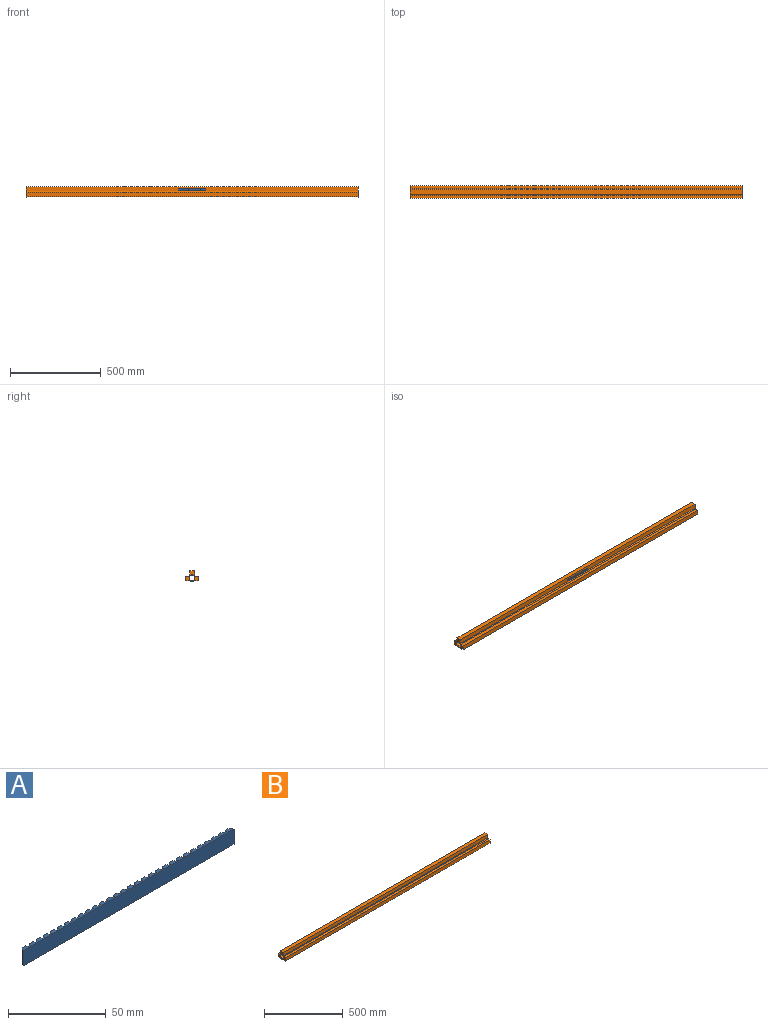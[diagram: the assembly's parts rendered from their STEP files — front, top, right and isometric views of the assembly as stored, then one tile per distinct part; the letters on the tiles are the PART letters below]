
ASSEMBLY  parts=2 mates=1
PART A: 126 faces, bbox 152.4x2.3x9.5 mm
  f0: plane 9.53x2.51mm, normal (0,1,0), area 24mm2, adj f33,f34,f121,f125
  f1: plane 9.53x2.51mm, normal (0,1,0), area 24mm2, adj f33,f34,f118,f123
  f2: plane 9.53x2.51mm, normal (0,1,0), area 24mm2, adj f33,f34,f115,f120
  f3: plane 9.53x2.51mm, normal (0,1,0), area 24mm2, adj f33,f34,f112,f117
  f4: plane 9.53x2.51mm, normal (0,1,0), area 24mm2, adj f33,f34,f109,f114
  f5: plane 9.53x2.51mm, normal (0,1,0), area 24mm2, adj f33,f34,f106,f111
  f6: plane 9.53x2.51mm, normal (0,1,0), area 24mm2, adj f33,f34,f103,f108
  f7: plane 9.53x2.51mm, normal (0,1,0), area 24mm2, adj f33,f34,f100,f105
  f8: plane 9.53x2.51mm, normal (0,1,0), area 24mm2, adj f33,f34,f97,f102
  f9: plane 9.53x2.51mm, normal (0,1,0), area 24mm2, adj f33,f34,f94,f99
  f10: plane 9.53x2.51mm, normal (0,1,0), area 24mm2, adj f33,f34,f91,f96
  f11: plane 9.53x2.51mm, normal (0,1,0), area 24mm2, adj f33,f34,f88,f93
  f12: plane 9.53x2.51mm, normal (0,1,0), area 24mm2, adj f33,f34,f85,f90
  f13: plane 9.53x2.51mm, normal (0,1,0), area 24mm2, adj f33,f34,f82,f87
  f14: plane 9.53x2.51mm, normal (0,1,0), area 24mm2, adj f33,f34,f79,f84
  f15: plane 9.53x2.51mm, normal (0,1,0), area 24mm2, adj f33,f34,f76,f81
  f16: plane 9.53x2.51mm, normal (0,1,0), area 24mm2, adj f33,f34,f73,f78
  f17: plane 9.53x2.51mm, normal (0,1,0), area 24mm2, adj f33,f34,f70,f75
  f18: plane 9.53x2.51mm, normal (0,1,0), area 24mm2, adj f33,f34,f67,f72
  f19: plane 9.53x2.51mm, normal (0,1,0), area 24mm2, adj f33,f34,f64,f69
  f20: plane 9.53x2.51mm, normal (0,1,0), area 24mm2, adj f33,f34,f61,f66
  f21: plane 9.53x2.51mm, normal (0,1,0), area 24mm2, adj f33,f34,f58,f63
  f22: plane 9.53x2.51mm, normal (0,1,0), area 24mm2, adj f33,f34,f55,f60
  f23: plane 9.53x2.51mm, normal (0,1,0), area 24mm2, adj f33,f34,f52,f57
  f24: plane 9.53x2.51mm, normal (0,1,0), area 24mm2, adj f33,f34,f49,f54
  f25: plane 9.53x2.51mm, normal (0,1,0), area 24mm2, adj f33,f34,f46,f51
  f26: plane 9.53x2.51mm, normal (0,1,0), area 24mm2, adj f33,f34,f43,f48
  f27: plane 9.53x2.51mm, normal (0,1,0), area 24mm2, adj f33,f34,f40,f45
  f28: plane 9.53x2.51mm, normal (0,1,0), area 24mm2, adj f33,f34,f37,f42
  f29: plane 9.53x1.02mm, normal (-1,0,0), area 9.7mm2, adj f30,f33,f34,f35
  f30: plane 152.4x9.53mm, normal (0,-1,0), area 1451.6mm2, adj f29,f31,f33,f34
  f31: plane 9.53x1.02mm, normal (1,0,0), area 9.7mm2, adj f30,f33,f34,f124
  f32: plane 9.53x2.51mm, normal (0,1,0), area 24mm2, adj f33,f34,f36,f39
  f33: plane 152.4x2.29mm, normal (0,0,1), area 273.2mm2, adj f0,f1,f2,f3,f4,f5,f6,f7
  f34: plane 152.4x2.29mm, normal (0,0,-1), area 273.2mm2, adj f0,f1,f2,f3,f4,f5,f6,f7
  f35: plane 9.53x0.69mm, normal (0,1,0), area 6.6mm2, adj f29,f33,f34,f36
  f36: plane 9.53x1.27mm, normal (-0.91,0.42,0), area 13.3mm2, adj f32,f33,f34,f35
  f37: plane 9.53x1.27mm, normal (-0.91,0.42,0), area 13.3mm2, adj f28,f33,f34,f38
  f38: plane 9.53x1.38mm, normal (0,1,0), area 13.2mm2, adj f33,f34,f37,f39
  f39: plane 9.53x1.27mm, normal (0.91,0.42,0), area 13.3mm2, adj f32,f33,f34,f38
  f40: plane 9.53x1.27mm, normal (-0.91,0.42,0), area 13.3mm2, adj f27,f33,f34,f41
  f41: plane 9.53x1.38mm, normal (0,1,0), area 13.2mm2, adj f33,f34,f40,f42
  f42: plane 9.53x1.27mm, normal (0.91,0.42,0), area 13.3mm2, adj f28,f33,f34,f41
  f43: plane 9.53x1.27mm, normal (-0.91,0.42,0), area 13.3mm2, adj f26,f33,f34,f44
  f44: plane 9.53x1.38mm, normal (0,1,0), area 13.2mm2, adj f33,f34,f43,f45
  f45: plane 9.53x1.27mm, normal (0.91,0.42,0), area 13.3mm2, adj f27,f33,f34,f44
  f46: plane 9.53x1.27mm, normal (-0.91,0.42,0), area 13.3mm2, adj f25,f33,f34,f47
  f47: plane 9.53x1.38mm, normal (0,1,0), area 13.2mm2, adj f33,f34,f46,f48
  f48: plane 9.53x1.27mm, normal (0.91,0.42,0), area 13.3mm2, adj f26,f33,f34,f47
  f49: plane 9.53x1.27mm, normal (-0.91,0.42,0), area 13.3mm2, adj f24,f33,f34,f50
  f50: plane 9.53x1.38mm, normal (0,1,0), area 13.2mm2, adj f33,f34,f49,f51
  f51: plane 9.53x1.27mm, normal (0.91,0.42,0), area 13.3mm2, adj f25,f33,f34,f50
  f52: plane 9.53x1.27mm, normal (-0.91,0.42,0), area 13.3mm2, adj f23,f33,f34,f53
  f53: plane 9.53x1.38mm, normal (0,1,0), area 13.2mm2, adj f33,f34,f52,f54
  f54: plane 9.53x1.27mm, normal (0.91,0.42,0), area 13.3mm2, adj f24,f33,f34,f53
  f55: plane 9.53x1.27mm, normal (-0.91,0.42,0), area 13.3mm2, adj f22,f33,f34,f56
  f56: plane 9.53x1.38mm, normal (0,1,0), area 13.2mm2, adj f33,f34,f55,f57
  f57: plane 9.53x1.27mm, normal (0.91,0.42,0), area 13.3mm2, adj f23,f33,f34,f56
  f58: plane 9.53x1.27mm, normal (-0.91,0.42,0), area 13.3mm2, adj f21,f33,f34,f59
  f59: plane 9.53x1.38mm, normal (0,1,0), area 13.2mm2, adj f33,f34,f58,f60
  f60: plane 9.53x1.27mm, normal (0.91,0.42,0), area 13.3mm2, adj f22,f33,f34,f59
  f61: plane 9.53x1.27mm, normal (-0.91,0.42,0), area 13.3mm2, adj f20,f33,f34,f62
  f62: plane 9.53x1.38mm, normal (0,1,0), area 13.2mm2, adj f33,f34,f61,f63
  f63: plane 9.53x1.27mm, normal (0.91,0.42,0), area 13.3mm2, adj f21,f33,f34,f62
  f64: plane 9.53x1.27mm, normal (-0.91,0.42,0), area 13.3mm2, adj f19,f33,f34,f65
  f65: plane 9.53x1.38mm, normal (0,1,0), area 13.2mm2, adj f33,f34,f64,f66
  f66: plane 9.53x1.27mm, normal (0.91,0.42,0), area 13.3mm2, adj f20,f33,f34,f65
  f67: plane 9.53x1.27mm, normal (-0.91,0.42,0), area 13.3mm2, adj f18,f33,f34,f68
  f68: plane 9.53x1.38mm, normal (0,1,0), area 13.2mm2, adj f33,f34,f67,f69
  f69: plane 9.53x1.27mm, normal (0.91,0.42,0), area 13.3mm2, adj f19,f33,f34,f68
  f70: plane 9.53x1.27mm, normal (-0.91,0.42,0), area 13.3mm2, adj f17,f33,f34,f71
  f71: plane 9.53x1.38mm, normal (0,1,0), area 13.2mm2, adj f33,f34,f70,f72
  f72: plane 9.53x1.27mm, normal (0.91,0.42,0), area 13.3mm2, adj f18,f33,f34,f71
  f73: plane 9.53x1.27mm, normal (-0.91,0.42,0), area 13.3mm2, adj f16,f33,f34,f74
  f74: plane 9.53x1.38mm, normal (0,1,0), area 13.2mm2, adj f33,f34,f73,f75
  f75: plane 9.53x1.27mm, normal (0.91,0.42,0), area 13.3mm2, adj f17,f33,f34,f74
  f76: plane 9.53x1.27mm, normal (-0.91,0.42,0), area 13.3mm2, adj f15,f33,f34,f77
  f77: plane 9.53x1.38mm, normal (0,1,0), area 13.2mm2, adj f33,f34,f76,f78
  f78: plane 9.53x1.27mm, normal (0.91,0.42,0), area 13.3mm2, adj f16,f33,f34,f77
  f79: plane 9.53x1.27mm, normal (-0.91,0.42,0), area 13.3mm2, adj f14,f33,f34,f80
  f80: plane 9.53x1.38mm, normal (0,1,0), area 13.2mm2, adj f33,f34,f79,f81
  f81: plane 9.53x1.27mm, normal (0.91,0.42,0), area 13.3mm2, adj f15,f33,f34,f80
  f82: plane 9.53x1.27mm, normal (-0.91,0.42,0), area 13.3mm2, adj f13,f33,f34,f83
  f83: plane 9.53x1.38mm, normal (0,1,0), area 13.2mm2, adj f33,f34,f82,f84
  f84: plane 9.53x1.27mm, normal (0.91,0.42,0), area 13.3mm2, adj f14,f33,f34,f83
  f85: plane 9.53x1.27mm, normal (-0.91,0.42,0), area 13.3mm2, adj f12,f33,f34,f86
  f86: plane 9.53x1.38mm, normal (0,1,0), area 13.2mm2, adj f33,f34,f85,f87
  f87: plane 9.53x1.27mm, normal (0.91,0.42,0), area 13.3mm2, adj f13,f33,f34,f86
  f88: plane 9.53x1.27mm, normal (-0.91,0.42,0), area 13.3mm2, adj f11,f33,f34,f89
  f89: plane 9.53x1.38mm, normal (0,1,0), area 13.2mm2, adj f33,f34,f88,f90
  f90: plane 9.53x1.27mm, normal (0.91,0.42,0), area 13.3mm2, adj f12,f33,f34,f89
  f91: plane 9.53x1.27mm, normal (-0.91,0.42,0), area 13.3mm2, adj f10,f33,f34,f92
  f92: plane 9.53x1.38mm, normal (0,1,0), area 13.2mm2, adj f33,f34,f91,f93
  f93: plane 9.53x1.27mm, normal (0.91,0.42,0), area 13.3mm2, adj f11,f33,f34,f92
  f94: plane 9.53x1.27mm, normal (-0.91,0.42,0), area 13.3mm2, adj f9,f33,f34,f95
  f95: plane 9.53x1.38mm, normal (0,1,0), area 13.2mm2, adj f33,f34,f94,f96
  f96: plane 9.53x1.27mm, normal (0.91,0.42,0), area 13.3mm2, adj f10,f33,f34,f95
  f97: plane 9.53x1.27mm, normal (-0.91,0.42,0), area 13.3mm2, adj f8,f33,f34,f98
  f98: plane 9.53x1.38mm, normal (0,1,0), area 13.2mm2, adj f33,f34,f97,f99
  f99: plane 9.53x1.27mm, normal (0.91,0.42,0), area 13.3mm2, adj f9,f33,f34,f98
  f100: plane 9.53x1.27mm, normal (-0.91,0.42,0), area 13.3mm2, adj f7,f33,f34,f101
  f101: plane 9.53x1.38mm, normal (0,1,0), area 13.2mm2, adj f33,f34,f100,f102
  f102: plane 9.53x1.27mm, normal (0.91,0.42,0), area 13.3mm2, adj f8,f33,f34,f101
  f103: plane 9.53x1.27mm, normal (-0.91,0.42,0), area 13.3mm2, adj f6,f33,f34,f104
  f104: plane 9.53x1.38mm, normal (0,1,0), area 13.2mm2, adj f33,f34,f103,f105
  f105: plane 9.53x1.27mm, normal (0.91,0.42,0), area 13.3mm2, adj f7,f33,f34,f104
  f106: plane 9.53x1.27mm, normal (-0.91,0.42,0), area 13.3mm2, adj f5,f33,f34,f107
  f107: plane 9.53x1.38mm, normal (0,1,0), area 13.2mm2, adj f33,f34,f106,f108
  f108: plane 9.53x1.27mm, normal (0.91,0.42,0), area 13.3mm2, adj f6,f33,f34,f107
  f109: plane 9.53x1.27mm, normal (-0.91,0.42,0), area 13.3mm2, adj f4,f33,f34,f110
  f110: plane 9.53x1.38mm, normal (0,1,0), area 13.2mm2, adj f33,f34,f109,f111
  f111: plane 9.53x1.27mm, normal (0.91,0.42,0), area 13.3mm2, adj f5,f33,f34,f110
  f112: plane 9.53x1.27mm, normal (-0.91,0.42,0), area 13.3mm2, adj f3,f33,f34,f113
  f113: plane 9.53x1.38mm, normal (0,1,0), area 13.2mm2, adj f33,f34,f112,f114
  f114: plane 9.53x1.27mm, normal (0.91,0.42,0), area 13.3mm2, adj f4,f33,f34,f113
  f115: plane 9.53x1.27mm, normal (-0.91,0.42,0), area 13.3mm2, adj f2,f33,f34,f116
  f116: plane 9.53x1.38mm, normal (0,1,0), area 13.2mm2, adj f33,f34,f115,f117
  f117: plane 9.53x1.27mm, normal (0.91,0.42,0), area 13.3mm2, adj f3,f33,f34,f116
  f118: plane 9.53x1.27mm, normal (-0.91,0.42,0), area 13.3mm2, adj f1,f33,f34,f119
  f119: plane 9.53x1.38mm, normal (0,1,0), area 13.2mm2, adj f33,f34,f118,f120
  f120: plane 9.53x1.27mm, normal (0.91,0.42,0), area 13.3mm2, adj f2,f33,f34,f119
  f121: plane 9.53x1.27mm, normal (-0.91,0.42,0), area 13.3mm2, adj f0,f33,f34,f122
  f122: plane 9.53x1.38mm, normal (0,1,0), area 13.2mm2, adj f33,f34,f121,f123
  f123: plane 9.53x1.27mm, normal (0.91,0.42,0), area 13.3mm2, adj f1,f33,f34,f122
  f124: plane 9.53x0.69mm, normal (0,1,0), area 6.6mm2, adj f31,f33,f34,f125
  f125: plane 9.53x1.27mm, normal (0.91,0.42,0), area 13.3mm2, adj f0,f33,f34,f124
PART B: 15 faces, bbox 1828.8x69.4x58.6 mm
  f0: plane 1828.8x25.4mm, normal (0,1,0), area 46451.5mm2, adj f1,f11,f13,f14
  f1: plane 1828.8x17.78mm, normal (0,0,1), area 32516.1mm2, adj f0,f2,f13,f14
  f2: cylinder r=19.05mm len=1828.8mm, axis (-1,0,0), area 12635.5mm2, adj f1,f3,f13,f14
  f3: plane 1828.8x25.4mm, normal (0,1,0), area 46451.5mm2, adj f2,f4,f13,f14
  f4: plane 1828.8x25.4mm, normal (0,0,1), area 46451.5mm2, adj f3,f5,f13,f14
  f5: plane 1828.8x25.4mm, normal (0,-1,0), area 46451.5mm2, adj f4,f6,f13,f14
  f6: cylinder r=19.05mm len=1828.8mm, axis (-1,0,0), area 12635.5mm2, adj f5,f7,f13,f14
  f7: plane 1828.8x17.78mm, normal (0,0,1), area 32516.1mm2, adj f6,f8,f13,f14
  f8: plane 1828.8x25.4mm, normal (0,-1,0), area 46451.5mm2, adj f7,f9,f13,f14
  f9: plane 1828.8x25.4mm, normal (0,0,-1), area 46451.5mm2, adj f8,f10,f13,f14
  f10: cylinder r=19.05mm len=1828.8mm, axis (-1,0,0), area 35500.5mm2, adj f9,f11,f13,f14
  f11: plane 1828.8x25.4mm, normal (0,0,-1), area 46451.5mm2, adj f0,f10,f13,f14
  f12: cylinder r=16mm len=1828.8mm, axis (-1,0,0), area 183874mm2, adj f13,f14
  f13: plane 69.38x58.65mm, normal (1,0,0), area 1797.1mm2, adj f0,f1,f2,f3,f4,f5,f6,f7
  f14: plane 69.38x58.65mm, normal (-1,0,0), area 1797.1mm2, adj f0,f1,f2,f3,f4,f5,f6,f7
PLACE A rot(axis=(-1,0,0),180deg) t=(520.98,229.4,-142.16)mm
PLACE B t=(-317.22,242.1,-171.92)mm
MATE planar A.f30 <-> B.f5  axis (0,1,0) through (597.18,229.4,-137.4)mm
